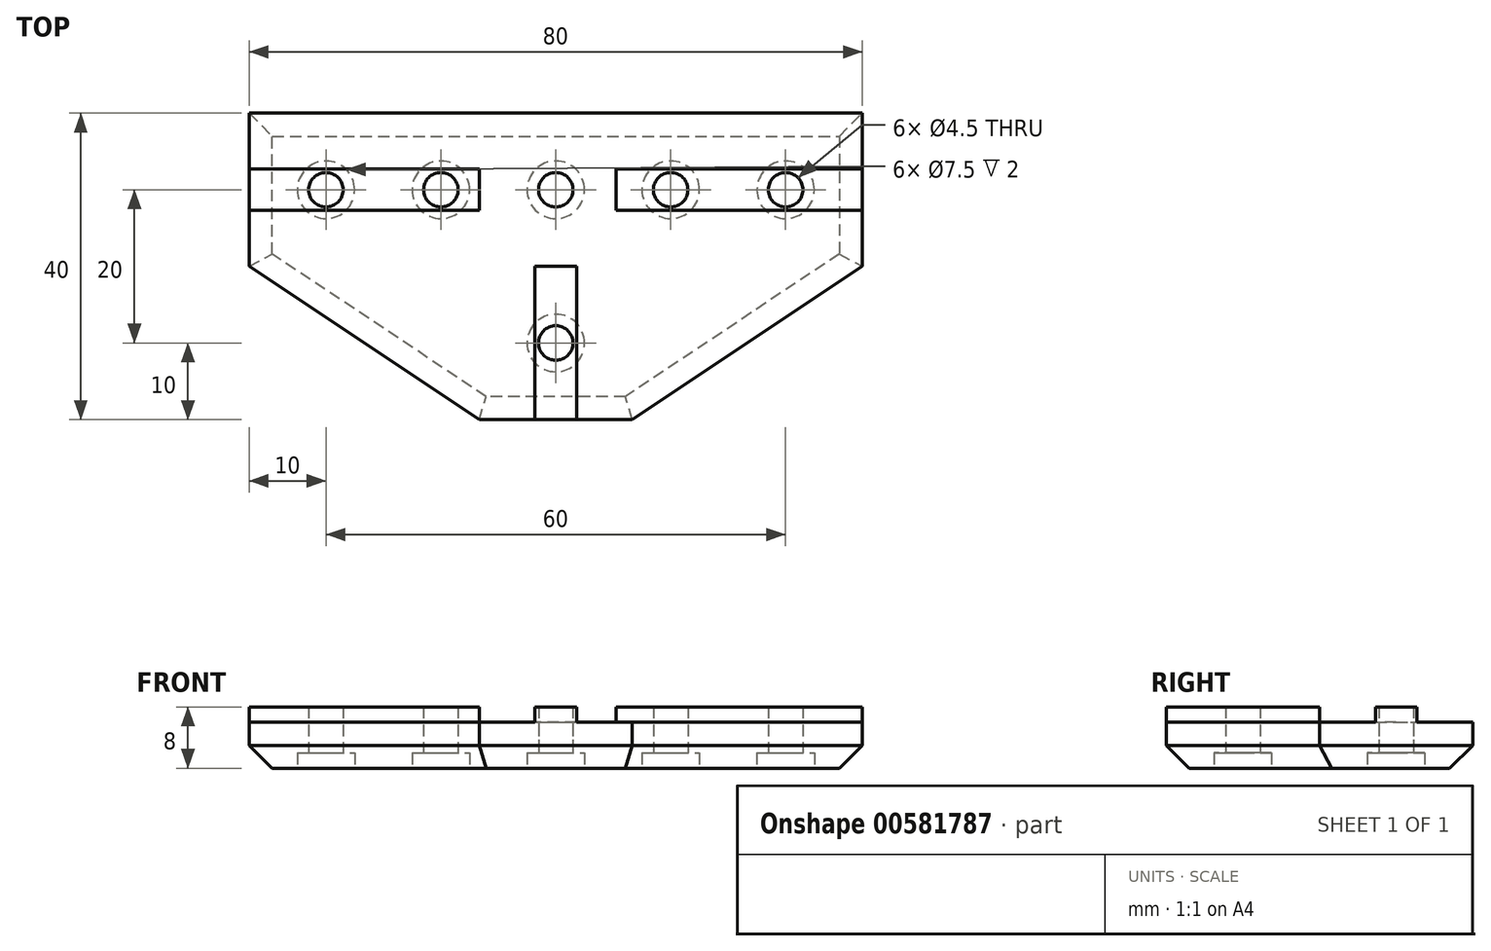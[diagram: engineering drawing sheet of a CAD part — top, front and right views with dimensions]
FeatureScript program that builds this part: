
annotation { "Feature Type Name" : "Feature", "Feature Type Description" : "" }
export const myFeature = defineFeature(function(context is Context, id is Id, definition is map)
    precondition{}
    {
        {
            var Q0;
            Q0=qCreatedBy(makeId("Top.planeOp"),FACE);
            var sketch = newSketch(context, id + "F0", { "sketchPlane" : qUnion([Q0])});
            skLineSegment(sketch, "E0", {"start": v(0, 0) * mm, "end": v(0, 20) * mm, "construction": true});
            skLineSegment(sketch, "E1", {"start": v(0, 0) * mm, "end": v(0, -20) * mm, "construction": true});
            skLineSegment(sketch, "E2", {"start": v(-10, 0) * mm, "end": v(-40, 0) * mm});
            skLineSegment(sketch, "E3", {"start": v(0, 20) * mm, "end": v(-40, 20) * mm});
            skLineSegment(sketch, "E4", {"start": v(-40, 20) * mm, "end": v(-40, 0) * mm});
            skLineSegment(sketch, "E5", {"start": v(0, 20) * mm, "end": v(40, 20) * mm});
            skLineSegment(sketch, "E6", {"start": v(40, 20) * mm, "end": v(40, 0) * mm});
            skLineSegment(sketch, "E7", {"start": v(40, 0) * mm, "end": v(10, 0) * mm});
            skLineSegment(sketch, "E8", {"start": v(0, -20) * mm, "end": v(10, -20) * mm});
            skLineSegment(sketch, "E9", {"start": v(10, -20) * mm, "end": v(10, 0) * mm});
            skLineSegment(sketch, "E10", {"start": v(0, -20) * mm, "end": v(-10, -20) * mm});
            skLineSegment(sketch, "E11", {"start": v(-10, -20) * mm, "end": v(-10, 0) * mm});
            skSolve(sketch);
        }
        {
            var Q0;
            Q0=qSketchRegion(id+"F0",true);
            extrude(context, id + "F1", {"entities" : qUnion([Q0]), "depth" : 6 * mm});
        }
        {
            var Q0;
            Q0=makeQuery(id+"F1.opExtrude","CAP_FACE",FACE,{"disambiguationData":[OSD([sQuery(id+"F0.wireOp",EDGE,"E2"),sQuery(id+"F0.wireOp",EDGE,"E3"),sQuery(id+"F0.wireOp",EDGE,"E4"),sQuery(id+"F0.wireOp",EDGE,"E5"),sQuery(id+"F0.wireOp",EDGE,"E6"),sQuery(id+"F0.wireOp",EDGE,"E7"),sQuery(id+"F0.wireOp",EDGE,"E8"),sQuery(id+"F0.wireOp",EDGE,"E9"),sQuery(id+"F0.wireOp",EDGE,"E10"),sQuery(id+"F0.wireOp",EDGE,"E11")])],"isStart":false});
            var sketch = newSketch(context, id + "F2", { "sketchPlane" : qUnion([Q0])});
            skLineSegment(sketch, "E12", {"start": v(-40, 10) * mm, "end": v(40, 10) * mm, "construction": true});
            skLineSegment(sketch, "E13", {"start": v(0, -20) * mm, "end": v(0, 0) * mm, "construction": true});
            skLineSegment(sketch, "E14", {"start": v(0, 0) * mm, "end": v(-2.71, 0) * mm});
            skLineSegment(sketch, "E15", {"start": v(-2.71, 0) * mm, "end": v(-2.7, -20) * mm});
            skLineSegment(sketch, "E16", {"start": v(2.71, -20) * mm, "end": v(2.71, 0) * mm});
            skLineSegment(sketch, "E17", {"start": v(2.71, 0) * mm, "end": v(0, 0) * mm});
            skLineSegment(sketch, "E18", {"start": v(-2.7, -20) * mm, "end": v(2.71, -20) * mm});
            skLineSegment(sketch, "E19", {"start": v(7.85, 10) * mm, "end": v(7.85, 12.71) * mm});
            skLineSegment(sketch, "E20", {"start": v(7.85, 12.71) * mm, "end": v(40, 12.71) * mm});
            skLineSegment(sketch, "E21", {"start": v(40, 12.7) * mm, "end": v(40, 7.3) * mm});
            skLineSegment(sketch, "E22", {"start": v(40, 7.3) * mm, "end": v(7.85, 7.29) * mm});
            skLineSegment(sketch, "E23", {"start": v(7.85, 7.29) * mm, "end": v(7.85, 10) * mm});
            skLineSegment(sketch, "E24", {"start": v(-40, 12.7) * mm, "end": v(-40, 7.29) * mm});
            skLineSegment(sketch, "E25", {"start": v(-40, 7.29) * mm, "end": v(-10, 7.29) * mm});
            skLineSegment(sketch, "E26", {"start": v(-10, 7.29) * mm, "end": v(-10, 12.71) * mm});
            skLineSegment(sketch, "E27", {"start": v(-10, 12.71) * mm, "end": v(-40, 12.71) * mm});
            skSolve(sketch);
        }
        {
            var Q0;
            Q0=qSketchRegion(id+"F2",true);
            extrude(context, id + "F3", {"entities" : qUnion([Q0]), "operationType" : NewBodyOperationType.ADD, "depth" : 2 * mm});
        }
        {
            var Q0;
            Q0=makeQuery(id+"F1.opExtrude","CAP_FACE",FACE,{"disambiguationData":[OSD([sQuery(id+"F0.wireOp",EDGE,"E2"),sQuery(id+"F0.wireOp",EDGE,"E3"),sQuery(id+"F0.wireOp",EDGE,"E4"),sQuery(id+"F0.wireOp",EDGE,"E5"),sQuery(id+"F0.wireOp",EDGE,"E6"),sQuery(id+"F0.wireOp",EDGE,"E7"),sQuery(id+"F0.wireOp",EDGE,"E8"),sQuery(id+"F0.wireOp",EDGE,"E9"),sQuery(id+"F0.wireOp",EDGE,"E10"),sQuery(id+"F0.wireOp",EDGE,"E11")])],"isStart":true});
            var sketch = newSketch(context, id + "F4", { "sketchPlane" : qUnion([Q0])});
            skCircle(sketch, "E28", {"center": v(-30, -10) * mm, "radius": 2.25 * mm});
            skCircle(sketch, "E29", {"center": v(0, -10) * mm, "radius": 2.25 * mm});
            skCircle(sketch, "E30", {"center": v(0, 10) * mm, "radius": 2.25 * mm});
            skCircle(sketch, "E31", {"center": v(30, -10) * mm, "radius": 2.25 * mm});
            skCircle(sketch, "E32", {"center": v(15, -10) * mm, "radius": 2.25 * mm});
            skCircle(sketch, "E33", {"center": v(-15, -10) * mm, "radius": 2.25 * mm});
            skSolve(sketch);
        }
        {
            var Q0;
            Q0=qSketchRegion(id+"F4",true);
            extrude(context, id + "F5", {"entities" : qUnion([Q0]), "operationType" : NewBodyOperationType.REMOVE, "endBound" : BoundingType.THROUGH_ALL, "oppositeDirection" : true, "depth" : 25 * mm});
        }
        {
            var Q0;
            Q0=makeQuery(id+"F1.opExtrude","CAP_FACE",FACE,{"disambiguationData":[OSD([sQuery(id+"F0.wireOp",EDGE,"E2"),sQuery(id+"F0.wireOp",EDGE,"E3"),sQuery(id+"F0.wireOp",EDGE,"E4"),sQuery(id+"F0.wireOp",EDGE,"E5"),sQuery(id+"F0.wireOp",EDGE,"E6"),sQuery(id+"F0.wireOp",EDGE,"E7"),sQuery(id+"F0.wireOp",EDGE,"E8"),sQuery(id+"F0.wireOp",EDGE,"E9"),sQuery(id+"F0.wireOp",EDGE,"E10"),sQuery(id+"F0.wireOp",EDGE,"E11")])],"isStart":true});
            var sketch = newSketch(context, id + "F6", { "sketchPlane" : qUnion([Q0])});
            skCircle(sketch, "E34", {"center": v(0, 10) * mm, "radius": 3.75 * mm});
            skCircle(sketch, "E35", {"center": v(0, -10) * mm, "radius": 3.75 * mm});
            skCircle(sketch, "E36", {"center": v(30, -10) * mm, "radius": 3.75 * mm});
            skCircle(sketch, "E37", {"center": v(-30, -10) * mm, "radius": 3.75 * mm});
            skCircle(sketch, "E38", {"center": v(-15, -10) * mm, "radius": 3.75 * mm});
            skCircle(sketch, "E39", {"center": v(15, -10) * mm, "radius": 3.75 * mm});
            skSolve(sketch);
        }
        {
            var Q0;
            Q0=qSketchRegion(id+"F6",true);
            extrude(context, id + "F7", {"entities" : qUnion([Q0]), "operationType" : NewBodyOperationType.REMOVE, "oppositeDirection" : true, "depth" : 2 * mm});
        }
        {
            var Q0;
            Q0=makeQuery(id+"F1.opExtrude","CAP_FACE",FACE,{"disambiguationData":[OSD([sQuery(id+"F0.wireOp",EDGE,"E2"),sQuery(id+"F0.wireOp",EDGE,"E3"),sQuery(id+"F0.wireOp",EDGE,"E4"),sQuery(id+"F0.wireOp",EDGE,"E5"),sQuery(id+"F0.wireOp",EDGE,"E6"),sQuery(id+"F0.wireOp",EDGE,"E7"),sQuery(id+"F0.wireOp",EDGE,"E8"),sQuery(id+"F0.wireOp",EDGE,"E9"),sQuery(id+"F0.wireOp",EDGE,"E10"),sQuery(id+"F0.wireOp",EDGE,"E11")])],"isStart":false});
            var sketch = newSketch(context, id + "F8", { "sketchPlane" : qUnion([Q0])});
            skLineSegment(sketch, "E40", {"start": v(-40, 0) * mm, "end": v(-10, -20) * mm});
            skLineSegment(sketch, "E41", {"start": v(-10, -20) * mm, "end": v(-10, 0) * mm});
            skLineSegment(sketch, "E42", {"start": v(-10, 0) * mm, "end": v(-40, 0) * mm});
            skLineSegment(sketch, "E43", {"start": v(10, -20) * mm, "end": v(10, 0) * mm});
            skLineSegment(sketch, "E44", {"start": v(10, 0) * mm, "end": v(40, 0) * mm});
            skLineSegment(sketch, "E45", {"start": v(40, 0) * mm, "end": v(10, -20) * mm});
            skSolve(sketch);
        }
        {
            var Q0;
            Q0=qSketchRegion(id+"F8",true);
            extrude(context, id + "F9", {"entities" : qUnion([Q0]), "operationType" : NewBodyOperationType.ADD, "oppositeDirection" : true, "depth" : 6 * mm});
        }
        {
            var Q0;
            Q0=makeQuery(id+"F9.opExtrude","CAP_EDGE",EDGE,{"disambiguationData":[OSD([sQuery(id+"F8.wireOp",EDGE,"E40")])],"isStart":false});
            var Q1;
            Q1=makeQuery(id+"F1.opExtrude","CAP_EDGE",EDGE,{"disambiguationData":[OSD([sQuery(id+"F0.wireOp",EDGE,"E8"),sQuery(id+"F0.wireOp",EDGE,"E10")])],"isStart":true});
            var Q2;
            Q2=makeQuery(id+"F9.opExtrude","CAP_EDGE",EDGE,{"disambiguationData":[OSD([sQuery(id+"F8.wireOp",EDGE,"E45")])],"isStart":false});
            var Q3;
            Q3=makeQuery(id+"F1.opExtrude","CAP_EDGE",EDGE,{"disambiguationData":[OSD([sQuery(id+"F0.wireOp",EDGE,"E6")])],"isStart":true});
            var Q4;
            Q4=makeQuery(id+"F1.opExtrude","CAP_EDGE",EDGE,{"disambiguationData":[OSD([sQuery(id+"F0.wireOp",EDGE,"E4")])],"isStart":true});
            var Q5;
            Q5=makeQuery(id+"F1.opExtrude","CAP_EDGE",EDGE,{"disambiguationData":[OSD([sQuery(id+"F0.wireOp",EDGE,"E3"),sQuery(id+"F0.wireOp",EDGE,"E5")])],"isStart":true});
            chamfer(context, id + "F10", {"entities" : qUnion([Q0, Q1, Q2, Q3, Q4, Q5]), "width" : 3 * mm, "tangentPropagation" : true});
        }
    });
